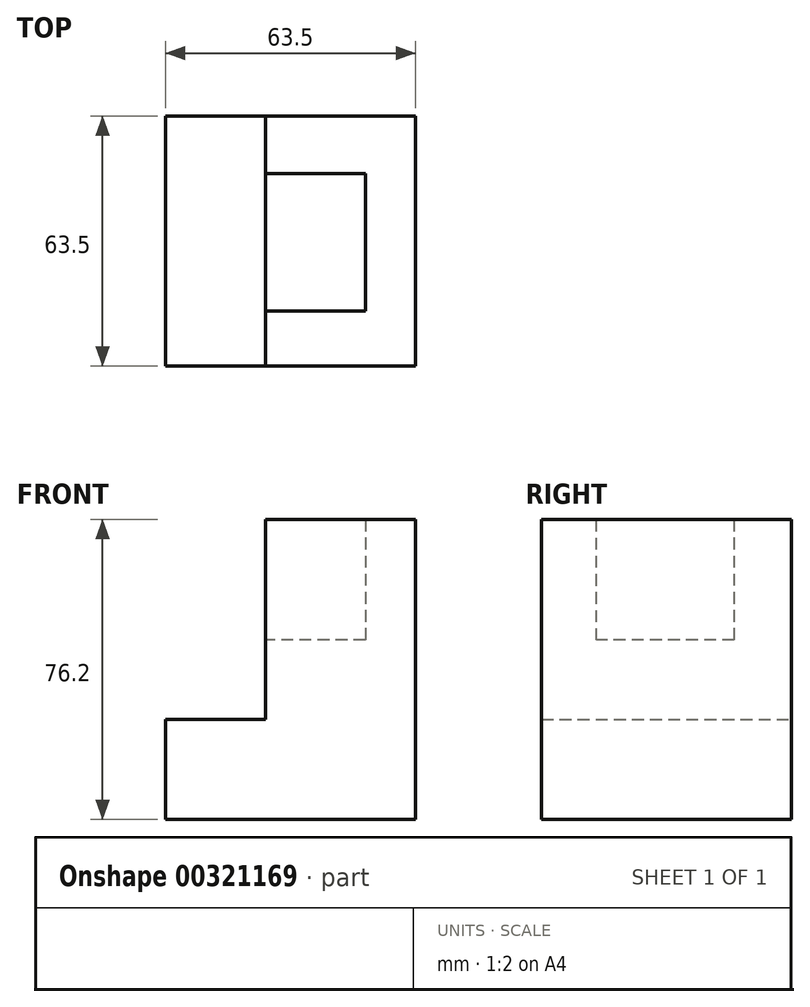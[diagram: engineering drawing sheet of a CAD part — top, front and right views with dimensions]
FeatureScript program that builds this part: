
annotation { "Feature Type Name" : "Feature", "Feature Type Description" : "" }
export const myFeature = defineFeature(function(context is Context, id is Id, definition is map)
    precondition{}
    {
        {
            var Q0;
            Q0=qCreatedBy(makeId("Front.planeOp"),FACE);
            var sketch = newSketch(context, id + "F0", { "sketchPlane" : qUnion([Q0])});
            skLineSegment(sketch, "E0", {"start": v(-55.01, -29.3) * mm, "end": v(-55.01, -3.9) * mm});
            skLineSegment(sketch, "E1", {"start": v(-55.01, -3.9) * mm, "end": v(-29.61, -3.9) * mm});
            skLineSegment(sketch, "E2", {"start": v(-29.61, -3.9) * mm, "end": v(-29.61, 46.9) * mm});
            skLineSegment(sketch, "E3", {"start": v(-29.61, 46.9) * mm, "end": v(8.49, 46.9) * mm});
            skLineSegment(sketch, "E4", {"start": v(8.49, 46.9) * mm, "end": v(8.49, -29.3) * mm});
            skLineSegment(sketch, "E5", {"start": v(8.49, -29.3) * mm, "end": v(-55.01, -29.3) * mm});
            skSolve(sketch);
        }
        {
            var Q0;
            Q0=makeQuery(id+"F0.imprint","IMPRINT",FACE,{"disambiguationData":[TD([[makeQuery(id+"F0.imprint","IMPRINT",EDGE,{"derivedFrom":sQuery(id+"F0.wireOp",EDGE,"E0")}),-1.0]])]});
            extrude(context, id + "F1", {"entities" : qUnion([Q0]), "depth" : 63.5 * mm});
        }
        {
            var Q0;
            Q0=makeQuery(id+"F1.opExtrude","SWEPT_FACE",FACE,{"disambiguationData":[OSD([sQuery(id+"F0.wireOp",EDGE,"E2")])]});
            var sketch = newSketch(context, id + "F2", { "sketchPlane" : qUnion([Q0])});
            skLineSegment(sketch, "E6", {"start": v(14.55, 46.9) * mm, "end": v(14.55, 16.25) * mm});
            skLineSegment(sketch, "E7", {"start": v(14.55, 16.25) * mm, "end": v(49.52, 16.25) * mm});
            skLineSegment(sketch, "E8", {"start": v(49.52, 16.25) * mm, "end": v(49.52, 46.9) * mm});
            skSolve(sketch);
        }
        {
            var Q0;
            {var subQ0=sQuery(id+"F2.wireOp",EDGE,"E6");Q0=makeQuery(id+"F2.imprint","IMPRINT",FACE,{"disambiguationData":[TD([[makeQuery(id+"F2.imprint","IMPRINT",EDGE,{"derivedFrom":subQ0}),1.0]])]});}
            extrude(context, id + "F3", {"entities" : qUnion([Q0]), "operationType" : NewBodyOperationType.REMOVE, "oppositeDirection" : true, "depth" : 25.4 * mm});
        }
    });
